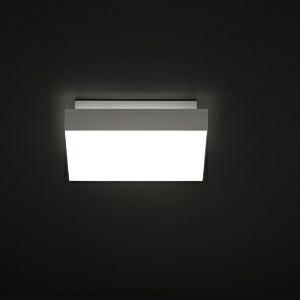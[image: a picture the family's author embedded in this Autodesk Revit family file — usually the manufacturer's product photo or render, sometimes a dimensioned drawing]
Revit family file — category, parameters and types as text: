
# Revit family: spectral_norea_norea-qa_312_2600_840_mps_d0c7
name_source: partatom
category: Lighting Fixtures
revit_build: Autodesk Revit 2016 (Build: 20150220_1215(x64)
units: mm (PartAtom-declared; Revit-internal decimal feet)

## family parameters
Cut with Voids When Loaded = No
Host = Face
Light Source = No
Part Type = Normal
Room Calculation Point = No
Round Connector Dimension = Use Diameter
Shared = No

## types (1)
- SPECTRAL NOREA (1 x )
    Apparent Load = 0 VA
    Approval mark = CE
    CIE Flux Codes = 64 90 97 96 69
    Control Gear = Electronic transformer
    Default Elevation = 1800 mm
    Description = SPT0000112
NOREA surface-mounted luminaire

Design:
Square luminaire element with a microprism panel in a natural anodised aluminium profile frame surround. The frame is suspended at the metal body. The LED module is formed as a square LED flat board and screwed to the luminaire element. For connection of the luminaire this can be hinged down and fastened with screws at an oblong hole in the powder-coated metal body. The indirect component is ensured by recesses in the top of the metal body. The metal body accommodates the electrical components and electronic ballast. Luminaire with heat-resistant wiring. Variant suitable for office use with a microprism panel MPS. The LED points are visible as circles on the microprism panel. Suitable for ceiling or wall mounting. Also in a dimmable version. Light colours 830 und 840. Protection rating IP20, safety class I.

Colour:
Housing – similar to RAL 9016 White silk matt;
Frame – natural anodised
    Height = 78 mm  [stored 0.255906 ft]
    Lamp = 1 x
    Lamp count = 1
    Length = 312 mm
    Luminous efficacy = 0 lm/W
    Manufacturer = Ridi
    ModVariant = No
    Model = NOREA-QA 312/2600/840 MPS
    Mounting Place = Ceiling
    Mounting Type = Surface mounted
    Number of Poles = 1
    OnlyDefault = Yes
    Power Factor = 1
    Product Name = SPECTRAL NOREA
    Product group = Ceiling mounted luminaire
    ProductGroupID = 3
    Protection Class = Protection class
    Protection Degree = IP 20
    RlxData = <blob elided: 31873 chars, md5=52b3375b>
    Socket = socket
    Standby Power = 0 W
    System Light Flux = 0 lm
    System Power = 0 W
    Type Image = leuchtstoffklein02_-_kopie.jpg
    URL = http://reluxnet.relux.com
    VarID = 1
    Voltage = 0 V
    Weight = 0.00 kg
    Width = 312 mm

note: [stored X ft] marks values corroborated as IEEE doubles in the binary element streams (Revit-internal decimal feet)

## geometry (parser evidence)
native form markers: Blend x4, Sweep x12
no freeform markers — native parametric forms only
